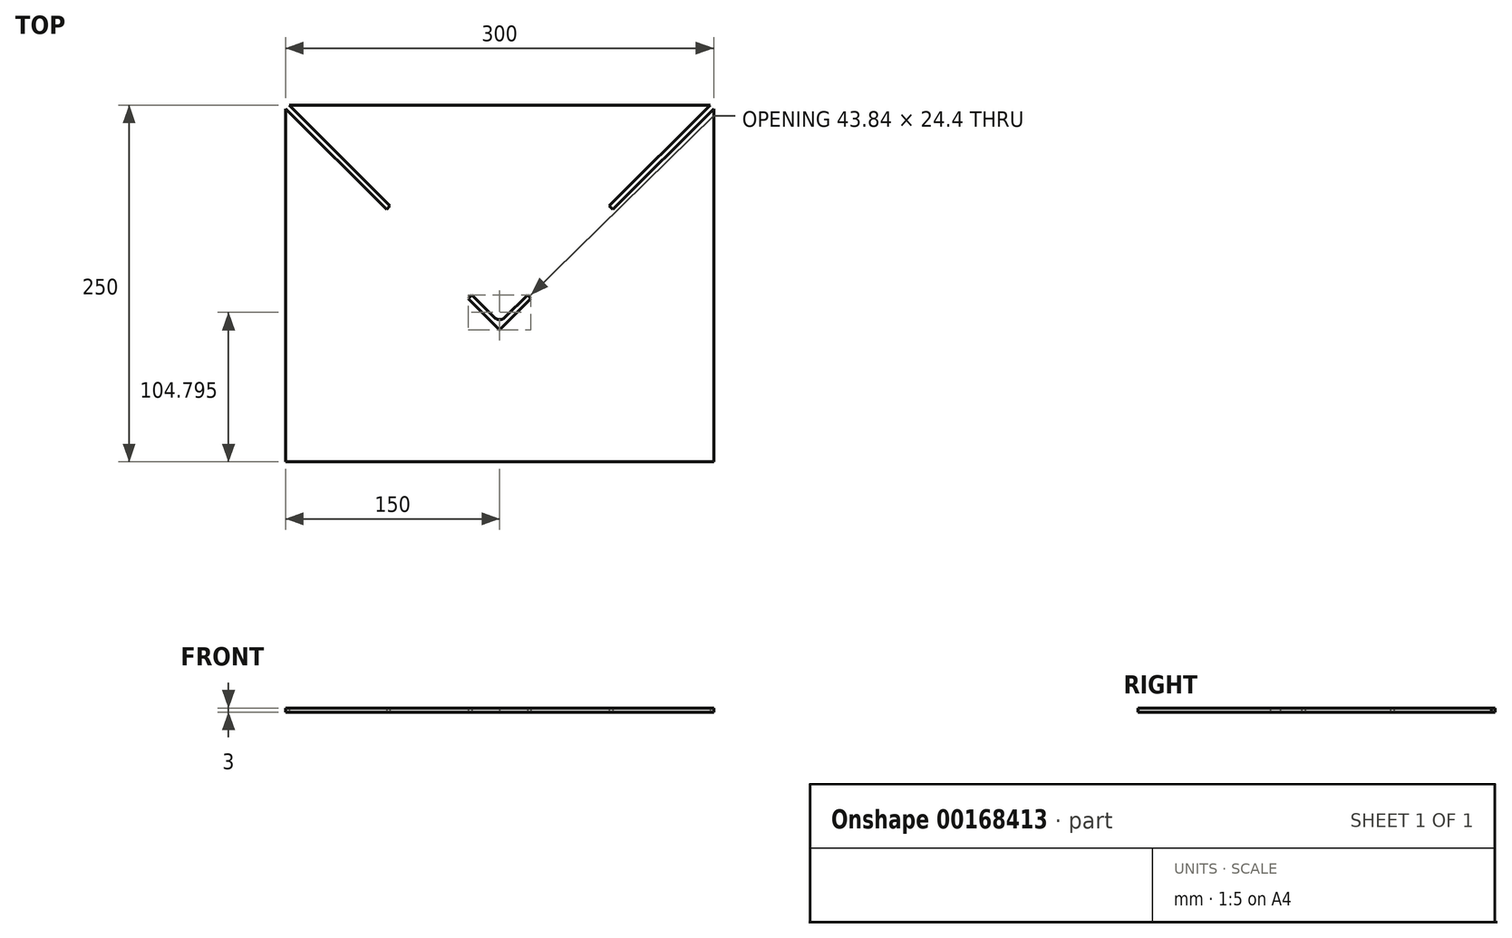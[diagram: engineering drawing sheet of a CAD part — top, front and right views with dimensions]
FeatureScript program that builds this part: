
annotation { "Feature Type Name" : "Feature", "Feature Type Description" : "" }
export const myFeature = defineFeature(function(context is Context, id is Id, definition is map)
    precondition{}
    {
        {
            var Q0;
            Q0=qCreatedBy(makeId("Top.planeOp"),FACE);
            var sketch = newSketch(context, id + "F0", { "sketchPlane" : qUnion([Q0])});
            skLineSegment(sketch, "E0.bottom", {"start": v(147.5, 83.68) * mm, "end": v(-147.5, 83.68) * mm});
            skLineSegment(sketch, "E0.top", {"start": v(150, -166.32) * mm, "end": v(-150, -166.32) * mm});
            skLineSegment(sketch, "E0.left", {"start": v(150, 81.23) * mm, "end": v(150, -166.32) * mm});
            skLineSegment(sketch, "E0.right", {"start": v(-150, 81.23) * mm, "end": v(-150, -166.32) * mm});
            skPoint(sketch, "E0.middle", {"position": v(0, -41.32) * mm});
            skLineSegment(sketch, "E1.0", {"start": v(-150, 81.23) * mm, "end": v(-79.29, 10.52) * mm});
            skPoint(sketch, "E2.orphan", {"position": v(-150, 83.68) * mm});
            skPoint(sketch, "E3.start.orphan", {"position": v(0, 155.23) * mm});
            skLineSegment(sketch, "E4", {"start": v(0, -166.32) * mm, "end": v(0, -66.32) * mm, "construction": true});
            skLineSegment(sketch, "E5.MirrorCS", {"start": v(150, 81.23) * mm, "end": v(79.29, 10.52) * mm});
            skPoint(sketch, "E6.orphan", {"position": v(150, 83.68) * mm});
            skLineSegment(sketch, "E7", {"start": v(-79.29, 10.52) * mm, "end": v(-3.54, -65.24) * mm, "construction": true});
            skLineSegment(sketch, "E8", {"start": v(79.29, 10.52) * mm, "end": v(3.54, -65.24) * mm, "construction": true});
            skLineSegment(sketch, "E9", {"start": v(-19.45, -49.33) * mm, "end": v(-3.54, -65.24) * mm});
            skLineSegment(sketch, "E10", {"start": v(3.54, -65.24) * mm, "end": v(19.45, -49.33) * mm});
            skLineSegment(sketch, "E11", {"start": v(19.45, -49.33) * mm, "end": v(21.92, -51.8) * mm});
            skLineSegment(sketch, "E12", {"start": v(21.92, -51.8) * mm, "end": v(0, -73.72) * mm});
            skLineSegment(sketch, "E13", {"start": v(0, -73.72) * mm, "end": v(-21.92, -51.8) * mm});
            skLineSegment(sketch, "E14", {"start": v(-21.92, -51.8) * mm, "end": v(-19.45, -49.33) * mm});
            skPoint(sketch, "E14.endSnap0", {"position": v(12.32, -81.09) * mm});
            skPoint(sketch, "E15.orphan", {"position": v(12.32, -17.57) * mm});
            skPoint(sketch, "E16.orphan", {"position": v(24.63, -93.4) * mm});
            skArc(sketch, "E17.filletArc", {"start": v(-3.54, -65.24) * mm, "mid": v(0, -66.7) * mm, "end": v(3.54, -65.24) * mm});
            skPoint(sketch, "E18.orphan", {"position": v(0, -68.77) * mm});
            skLineSegment(sketch, "E19.trimOffspring", {"start": v(87.17, 18.4) * mm, "end": v(-2.47, -71.25) * mm, "construction": true});
            skPoint(sketch, "E20.centerSnap0", {"position": v(150, 44.58) * mm});
            skPoint(sketch, "E20.center.orphan", {"position": v(121.34, 44.58) * mm});
            skPoint(sketch, "E21.orphan", {"position": v(-150, 255.48) * mm});
            skPoint(sketch, "E22.MirrorCS.end.orphan", {"position": v(79.29, 10.52) * mm});
            skPoint(sketch, "E23.MirrorCS.start.orphan", {"position": v(150, 255.48) * mm});
            skPoint(sketch, "E24.center.orphan", {"position": v(0, -201.5) * mm});
            skLineSegment(sketch, "E25.0", {"start": v(-147.5, 83.68) * mm, "end": v(-76.81, 13) * mm});
            skLineSegment(sketch, "E26.0", {"start": v(147.5, 83.68) * mm, "end": v(76.81, 13) * mm});
            skLineSegment(sketch, "E27", {"start": v(76.81, 13) * mm, "end": v(79.29, 10.52) * mm});
            skLineSegment(sketch, "E28", {"start": v(-76.81, 13) * mm, "end": v(-79.29, 10.52) * mm});
            skPoint(sketch, "E29.orphan", {"position": v(-152.45, 83.68) * mm});
            skPoint(sketch, "E30.orphan", {"position": v(152.45, 83.68) * mm});
            skSolve(sketch);
        }
        {
            var Q0;
            Q0 = qSketchRegion(id + "F0", true);
            extrude(context, id + "F1", {"entities" : qUnion([Q0]), "depth" : 3 * mm});
        }
    });
